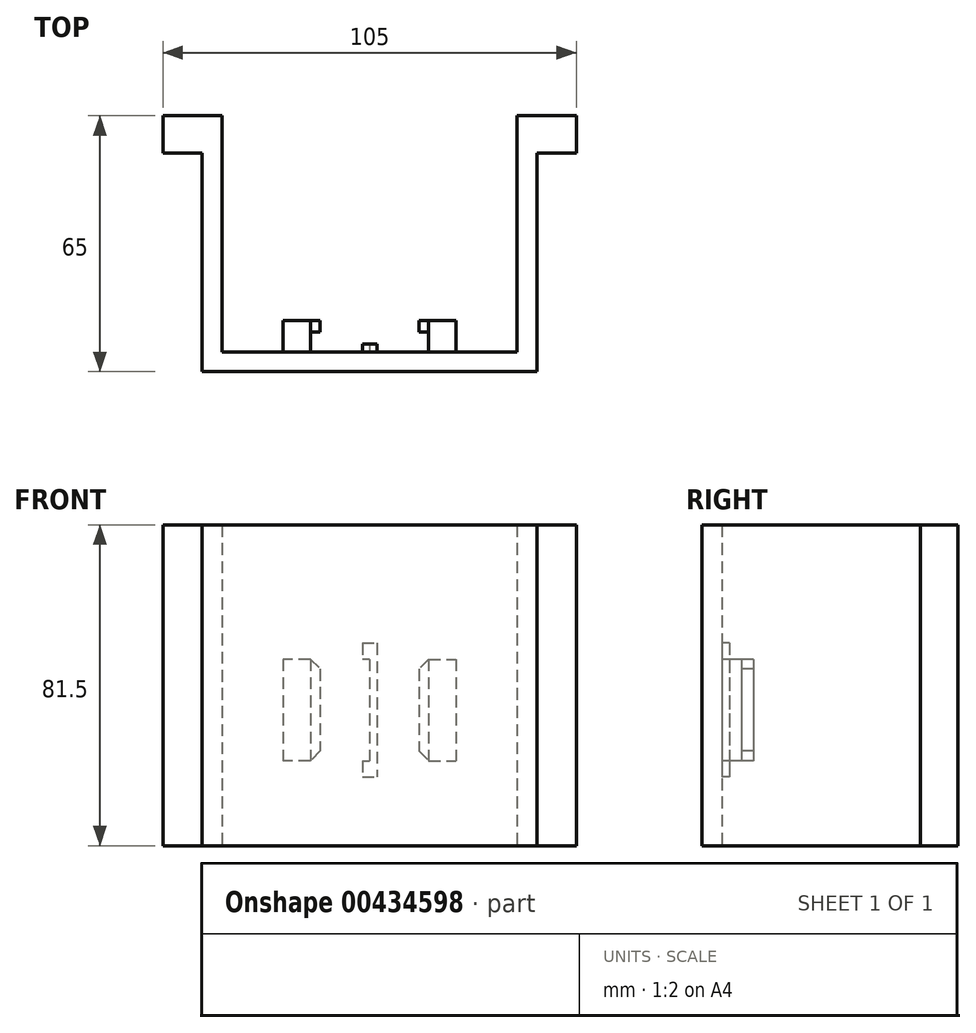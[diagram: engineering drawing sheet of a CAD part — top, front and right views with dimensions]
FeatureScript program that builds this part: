
annotation { "Feature Type Name" : "Feature", "Feature Type Description" : "" }
export const myFeature = defineFeature(function(context is Context, id is Id, definition is map)
    precondition{}
    {
        {
            var Q0;
            Q0=qCreatedBy(makeId("Top.planeOp"),FACE);
            var sketch = newSketch(context, id + "F0", { "sketchPlane" : qUnion([Q0])});
            skLineSegment(sketch, "E0.bottom", {"start": v(0, 0) * mm, "end": v(10, 0) * mm});
            skLineSegment(sketch, "E0.right", {"start": v(10, 0) * mm, "end": v(10, 9.5) * mm});
            skLineSegment(sketch, "E1", {"start": v(-5, 9.5) * mm, "end": v(-5, -50.5) * mm});
            skLineSegment(sketch, "E2", {"start": v(-5, 9.5) * mm, "end": v(10, 9.5) * mm});
            skLineSegment(sketch, "E3", {"start": v(0, 0) * mm, "end": v(0, -55.5) * mm});
            skLineSegment(sketch, "E4", {"start": v(0, -55.5) * mm, "end": v(-85, -55.5) * mm});
            skLineSegment(sketch, "E5", {"start": v(-80, -50.5) * mm, "end": v(-5, -50.5) * mm});
            skLineSegment(sketch, "E6", {"start": v(-85, -55.5) * mm, "end": v(-85, 0) * mm});
            skLineSegment(sketch, "E7", {"start": v(-85, 0) * mm, "end": v(-95, 0) * mm});
            skLineSegment(sketch, "E8", {"start": v(-95, 0) * mm, "end": v(-95, 9.5) * mm});
            skLineSegment(sketch, "E9", {"start": v(-95, 9.5) * mm, "end": v(-80, 9.5) * mm});
            skLineSegment(sketch, "E10", {"start": v(-80, 9.5) * mm, "end": v(-80, -50.5) * mm});
            skSolve(sketch);
        }
        {
            var Q0;
            Q0=makeQuery(id+"F0.imprint","IMPRINT",FACE,{"disambiguationData":[TD([[makeQuery(id+"F0.imprint","IMPRINT",EDGE,{"derivedFrom":sQuery(id+"F0.wireOp",EDGE,"E0.bottom")}),1.0]])]});
            extrude(context, id + "F1", {"entities" : qUnion([Q0]), "depth" : 81.5 * mm});
        }
        {
            var Q0;
            Q0=makeQuery(id+"F1.opExtrude","SWEPT_FACE",FACE,{"disambiguationData":[OSD([sQuery(id+"F0.wireOp",EDGE,"E5")])]});
            var sketch = newSketch(context, id + "F2", { "sketchPlane" : qUnion([Q0])});
            skLineSegment(sketch, "E11", {"start": v(42.5, 81.5) * mm, "end": v(42.5, 0) * mm});
            skLineSegment(sketch, "E12", {"start": v(42.5, 51.5) * mm, "end": v(42.5, 17.5) * mm});
            skLineSegment(sketch, "E13.bottom", {"start": v(42.5, 51.5) * mm, "end": v(44.35, 51.5) * mm});
            skLineSegment(sketch, "E13.top", {"start": v(42.5, 17.5) * mm, "end": v(44.35, 17.5) * mm});
            skLineSegment(sketch, "E13.right", {"start": v(44.35, 51.5) * mm, "end": v(44.35, 17.5) * mm});
            skLineSegment(sketch, "E14", {"start": v(42.5, 47.4) * mm, "end": v(57.5, 47.4) * mm});
            skLineSegment(sketch, "E15", {"start": v(57.5, 47.4) * mm, "end": v(57.5, 21.6) * mm});
            skLineSegment(sketch, "E16", {"start": v(57.5, 21.6) * mm, "end": v(42.5, 21.6) * mm});
            skLineSegment(sketch, "E17", {"start": v(57.5, 47.4) * mm, "end": v(64.5, 47.4) * mm});
            skLineSegment(sketch, "E18", {"start": v(64.5, 47.4) * mm, "end": v(64.5, 21.6) * mm});
            skLineSegment(sketch, "E19", {"start": v(57.5, 21.6) * mm, "end": v(64.5, 21.6) * mm});
            skLineSegment(sketch, "E20", {"start": v(57.5, 47.4) * mm, "end": v(55.05, 44.95) * mm});
            skLineSegment(sketch, "E21", {"start": v(55.05, 44.95) * mm, "end": v(55.05, 24.05) * mm});
            skLineSegment(sketch, "E22", {"start": v(55.05, 24.05) * mm, "end": v(57.5, 21.6) * mm});
            skLineSegment(sketch, "E23.MirrorCS", {"start": v(40.65, 51.5) * mm, "end": v(40.65, 17.5) * mm});
            skLineSegment(sketch, "E24.MirrorCS", {"start": v(42.5, 51.5) * mm, "end": v(40.65, 51.5) * mm});
            skLineSegment(sketch, "E25.MirrorCS", {"start": v(42.5, 17.5) * mm, "end": v(40.65, 17.5) * mm});
            skLineSegment(sketch, "E26.MirrorCS", {"start": v(29.95, 44.95) * mm, "end": v(29.95, 24.05) * mm});
            skLineSegment(sketch, "E27.MirrorCS", {"start": v(27.5, 47.4) * mm, "end": v(29.95, 44.95) * mm});
            skLineSegment(sketch, "E28.MirrorCS", {"start": v(27.5, 47.4) * mm, "end": v(27.5, 21.6) * mm});
            skLineSegment(sketch, "E29.MirrorCS", {"start": v(29.95, 24.05) * mm, "end": v(27.5, 21.6) * mm});
            skLineSegment(sketch, "E30.MirrorCS", {"start": v(27.5, 21.6) * mm, "end": v(20.5, 21.6) * mm});
            skLineSegment(sketch, "E31.MirrorCS", {"start": v(20.5, 47.4) * mm, "end": v(20.5, 21.6) * mm});
            skLineSegment(sketch, "E32.MirrorCS", {"start": v(27.5, 47.4) * mm, "end": v(20.5, 47.4) * mm});
            skSolve(sketch);
        }
        {
            var Q0;
            Q0=makeQuery(id+"F2.imprint","IMPRINT",FACE,{"disambiguationData":[TD([[makeQuery(id+"F2.imprint","IMPRINT",EDGE,{"derivedFrom":sQuery(id+"F2.wireOp",EDGE,"E23.MirrorCS")}),1.0]])]});
            var Q1;
            {var subQ0=sQuery(id+"F2.wireOp",EDGE,"E14");var subQ1=sQuery(id+"F2.wireOp",EDGE,"E12");var subQ2=makeQuery(id+"F2.imprint","INTERSECT",VERTEX,{"derivedFrom":[subQ1,subQ0]});Q1=makeQuery(id+"F2.imprint","IMPRINT",FACE,{"disambiguationData":[TD([[makeQuery(id+"F2.imprint","IMPRINT",EDGE,{"disambiguationData":[TD([[subQ2,-1.0]])],"derivedFrom":subQ1}),1.0]])]});}
            var Q2;
            {var subQ0=sQuery(id+"F2.wireOp",EDGE,"E13.bottom");Q2=makeQuery(id+"F2.imprint","IMPRINT",FACE,{"disambiguationData":[TD([[makeQuery(id+"F2.imprint","IMPRINT",EDGE,{"derivedFrom":subQ0}),-1.0]])]});}
            var Q3;
            {var subQ0=sQuery(id+"F2.wireOp",EDGE,"E13.top");Q3=makeQuery(id+"F2.imprint","IMPRINT",FACE,{"disambiguationData":[TD([[makeQuery(id+"F2.imprint","IMPRINT",EDGE,{"derivedFrom":subQ0}),1.0]])]});}
            extrude(context, id + "F3", {"entities" : qUnion([Q0, Q1, Q2, Q3]), "operationType" : NewBodyOperationType.ADD, "depth" : 1.95 * mm});
        }
        {
            var Q0;
            Q0=makeQuery(id+"F2.imprint","IMPRINT",FACE,{"disambiguationData":[TD([[makeQuery(id+"F2.imprint","IMPRINT",EDGE,{"derivedFrom":sQuery(id+"F2.wireOp",EDGE,"E15")}),1.0]])]});
            var Q1;
            Q1=makeQuery(id+"F2.imprint","IMPRINT",FACE,{"disambiguationData":[TD([[makeQuery(id+"F2.imprint","IMPRINT",EDGE,{"derivedFrom":sQuery(id+"F2.wireOp",EDGE,"E28.MirrorCS")}),-1.0]])]});
            extrude(context, id + "F4", {"entities" : qUnion([Q0, Q1]), "operationType" : NewBodyOperationType.ADD, "depth" : 8 * mm});
        }
        {
            var Q0;
            Q0=makeQuery(id+"F2.imprint","IMPRINT",FACE,{"disambiguationData":[TD([[makeQuery(id+"F2.imprint","IMPRINT",EDGE,{"derivedFrom":sQuery(id+"F2.wireOp",EDGE,"E26.MirrorCS")}),-1.0]])]});
            var Q1;
            Q1=makeQuery(id+"F2.imprint","IMPRINT",FACE,{"disambiguationData":[TD([[makeQuery(id+"F2.imprint","IMPRINT",EDGE,{"derivedFrom":sQuery(id+"F2.wireOp",EDGE,"E15")}),-1.0]])]});
            extrude(context, id + "F5", {"entities" : qUnion([Q0, Q1]), "operationType" : NewBodyOperationType.ADD, "depth" : 8 * mm, "hasSecondDirection" : true, "secondDirectionOppositeDirection" : false, "secondDirectionDepth" : 5 * mm});
        }
    });
